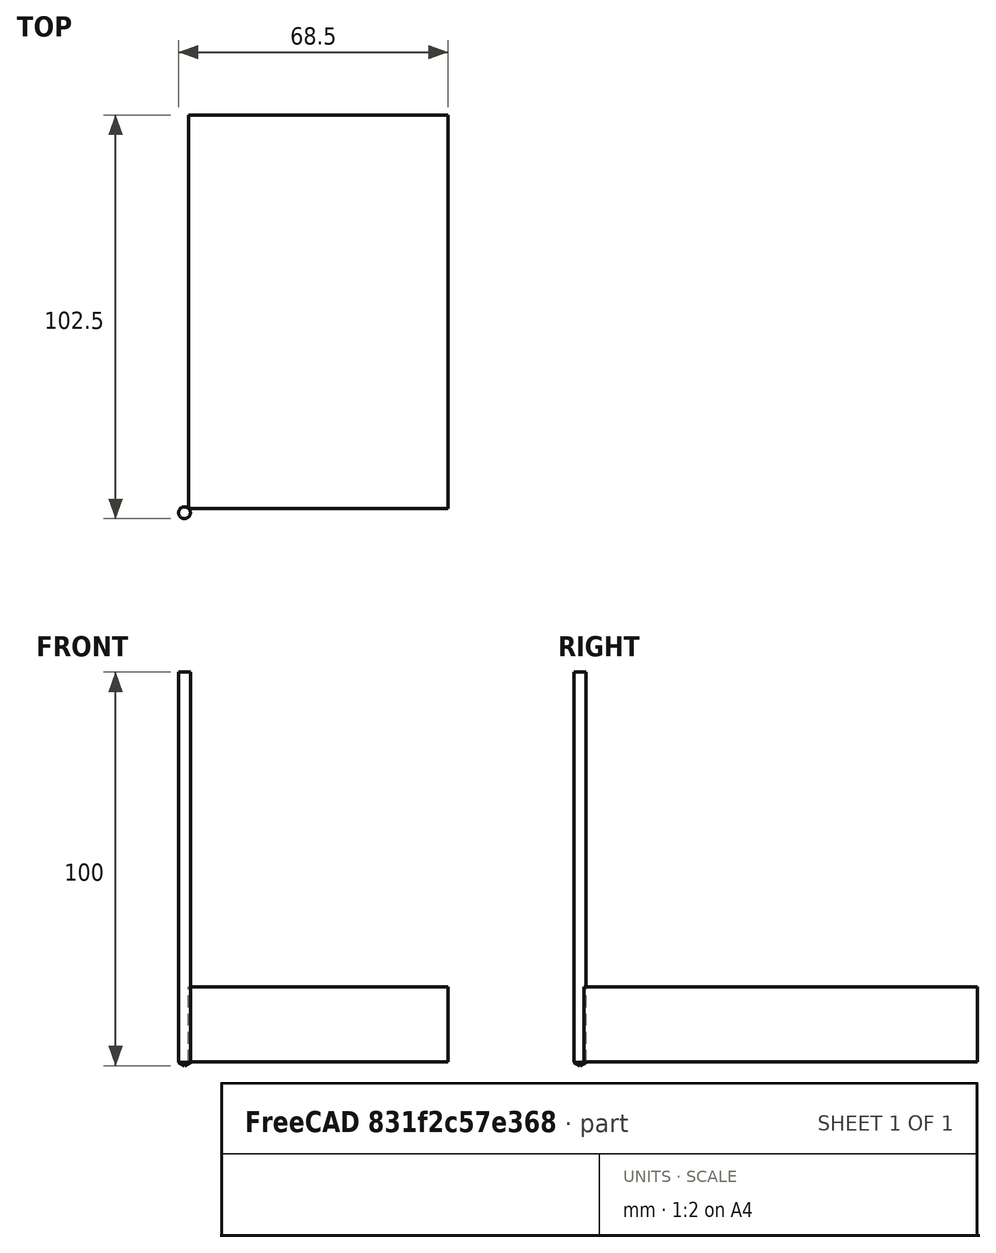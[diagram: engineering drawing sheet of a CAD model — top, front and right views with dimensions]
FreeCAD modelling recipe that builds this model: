
FCSTD DOCUMENT  (FreeCAD 1.0R39319 (Git))
Label: CNC test2
License: All rights reserved
LicenseURL: https://en.wikipedia.org/wiki/All_rights_reserved
objects: Path::FeaturePython×6, Sketcher::SketchObject×5, PartDesign::Pocket×4, Part::FeaturePython×3, App::DocumentObjectGroup×3, PartDesign::Pad×2, PartDesign::Body×1, App::FeaturePython×1, Mesh::Feature×1, Part::Feature×1, Part::Refine×1
note: 38 computed .brp shape members not serialized (recipe doc carries the construction recipe); baked Part::Feature solids carry a one-line shape summary decoded from their .brp

FEATURE [Sketcher::SketchObject] Sketch247
  ArcFitTolerance = 1e-06
  AttachmentSupport = -> [XY_Plane1079]
  FullyConstrained = true
  MakeInternals = false
  MapMode = 5
  sketch-geometry (14):
    g0: Circle [constr] CenterX=0 CenterY=0 CenterZ=0 NormalX=0 NormalY=0 NormalZ=1 AngleXU=0 Radius=12
    g1: LineSegment StartX=-3.45 StartY=2 StartZ=0 EndX=-3.45 EndY=18.25 EndZ=0
    g2: LineSegment StartX=-3.45 StartY=18.25 StartZ=0 EndX=3.45 EndY=18.25 EndZ=0
    g3: LineSegment StartX=3.45 StartY=18.25 StartZ=0 EndX=3.45 EndY=2 EndZ=0
    g4: LineSegment StartX=3.45 StartY=2 StartZ=0 EndX=9.95 EndY=2 EndZ=0
    g5: LineSegment StartX=9.95 StartY=2 StartZ=0 EndX=9.95 EndY=-2 EndZ=0
    g6: LineSegment StartX=9.95 StartY=-2 StartZ=0 EndX=3.45 EndY=-2 EndZ=0
    g7: LineSegment StartX=3.45 StartY=-2 StartZ=0 EndX=3.45 EndY=-18.25 EndZ=0
    g8: LineSegment StartX=3.45 StartY=-18.25 StartZ=0 EndX=-3.45 EndY=-18.25 EndZ=0
    g9: LineSegment StartX=-3.45 StartY=-18.25 StartZ=0 EndX=-3.45 EndY=-2 EndZ=0
    g10: LineSegment StartX=-3.45 StartY=-2 StartZ=0 EndX=-9.95 EndY=-2 EndZ=0
    g11: LineSegment StartX=-9.95 StartY=-2 StartZ=0 EndX=-9.95 EndY=2 EndZ=0
    g12: LineSegment StartX=-9.95 StartY=2 StartZ=0 EndX=-3.45 EndY=2 EndZ=0
    g13: Circle [constr] CenterX=0 CenterY=0 CenterZ=0 NormalX=0 NormalY=0 NormalZ=1 AngleXU=0 Radius=12
  constraints (39):
    c: Diameter(g0) = 24
    c: Coincident(g0,g-1)
    c: Vertical(g1)
    c: Coincident(g1,g2)
    c: Coincident(g2,g3)
    c: Vertical(g3)
    c: Coincident(g3,g4)
    c: Horizontal(g4)
    c: Coincident(g4,g5)
    c: Vertical(g5)
    c: Coincident(g5,g6)
    c: Horizontal(g6)
    c: Coincident(g6,g7)
    c: Vertical(g7)
    c: Coincident(g7,g8)
    c: Coincident(g8,g9)
    c: Vertical(g9)
    c: Coincident(g9,g10)
    c: Horizontal(g10)
    c: Coincident(g10,g11)
    c: Vertical(g11)
    c: Coincident(g11,g12)
    c: Coincident(g12,g1)
    c: Horizontal(g12)
    c: Horizontal(g8)
    c: Horizontal(g2)
    c: Equal(g3,g1)
    c: Equal(g1,g9)
    c: Equal(g9,g7)
    c: Equal(g6,g4)
    c: Equal(g4,g12)
    c: Equal(g12,g10)
    c: Distance(g2,g2) = 6.9
    c: DistanceY(g5,g5) = 4
    c: DistanceY(g3,g3) = 16.25
    c: DistanceX(g4,g4) = 6.5
    c: Symmetric(g1,g6,g0)
    c: Coincident(g13,g0)
    c: Equal(g13,g0)
FEATURE [PartDesign::Pad] Pad125
  Direction = (0,0,1)
  Length = 4
  Length2 = 10
  Profile = -> Sketch247
  ReferenceAxis = -> Sketch247 [N_Axis]
  Refine = true
  Suppressed = false
  Type = 0
FEATURE [Sketcher::SketchObject] Sketch248
  ArcFitTolerance = 1e-06
  AttachmentSupport = -> [Pad125]
  FullyConstrained = true
  MakeInternals = false
  MapMode = 5
  Placement = pos=(0,0,4) rot=(0,0,1;0rad)
  sketch-geometry (1):
    g0: Circle CenterX=0 CenterY=0 CenterZ=0 NormalX=0 NormalY=0 NormalZ=1 AngleXU=0 Radius=12
  constraints (2):
    c: Diameter(g0) = 24
    c: Coincident(g0,g-1)
FEATURE [PartDesign::Pad] Pad126
  BaseFeature = -> Pad125
  Direction = (0,0,1)
  Length = 12
  Length2 = 10
  Profile = -> Sketch248
  ReferenceAxis = -> Sketch248 [N_Axis]
  Refine = true
  Suppressed = false
  Type = 0
FEATURE [PartDesign::Pocket] Pocket089
  BaseFeature = -> Pad126
  Direction = (0,0,1)
  Length = 8
  Length2 = 5
  Profile = -> Pad126 [Face4]
  Refine = true
  Suppressed = false
  Type = 0
FEATURE [Sketcher::SketchObject] Sketch249
  ArcFitTolerance = 1e-06
  AttachmentSupport = -> [Pocket089]
  FullyConstrained = true
  MakeInternals = false
  MapMode = 5
  Placement = pos=(0,0,16) rot=(0,0,1;0rad)
  sketch-geometry (1):
    g0: Circle CenterX=0 CenterY=0 CenterZ=0 NormalX=0 NormalY=0 NormalZ=1 AngleXU=0 Radius=3.1
  constraints (2):
    c: Diameter(g0) = 6.2
    c: Coincident(g0,g-1)
FEATURE [PartDesign::Pocket] Pocket090
  BaseFeature = -> Pocket089
  Direction = (0,0,-1)
  Length = 5
  Length2 = 5
  Profile = -> Sketch249
  ReferenceAxis = -> Sketch249 [N_Axis]
  Refine = true
  Suppressed = false
  Type = 1
FEATURE [Sketcher::SketchObject] Sketch250
  ArcFitTolerance = 1e-06
  AttachmentSupport = -> [XZ_Plane1079]
  ExternalGeometry = -> [Pocket090]
  FullyConstrained = true
  MakeInternals = false
  MapMode = 5
  Placement = pos=(0,0,0) rot=(1,0,0;1.5708rad)
  sketch-geometry (1):
    g0: Circle CenterX=1e-16 CenterY=12 CenterZ=0 NormalX=0 NormalY=0 NormalZ=1 AngleXU=0 Radius=2.35
  constraints (2):
    c: Diameter(g0) = 4.7
    c: Symmetric(g-4,g-3,g0)
FEATURE [PartDesign::Pocket] Pocket091
  BaseFeature = -> Pocket090
  Direction = (0,1,-2e-16)
  Length = 5
  Length2 = 5
  Profile = -> Sketch250
  ReferenceAxis = -> Sketch250 [N_Axis]
  Refine = true
  Suppressed = false
  Type = 1
FEATURE [Sketcher::SketchObject] Sketch251
  ArcFitTolerance = 1e-06
  AttachmentSupport = -> [Pocket091]
  ExternalGeometry = -> [Pocket091]
  FullyConstrained = false
  MakeInternals = false
  MapMode = 5
  Placement = pos=(0,0,16) rot=(0,0,1;0rad)
  sketch-geometry (4):
    g0: LineSegment StartX=-5 StartY=10.9087 StartZ=0 EndX=5 EndY=10.9087 EndZ=0
    g1: LineSegment StartX=5 StartY=10.9087 StartZ=0 EndX=5 EndY=16.9794 EndZ=0
    g2: LineSegment StartX=5 StartY=16.9794 StartZ=0 EndX=-5 EndY=16.9794 EndZ=0
    g3: LineSegment StartX=-5 StartY=16.9794 StartZ=0 EndX=-5 EndY=10.9087 EndZ=0
  constraints (11):
    c: Coincident(g0,g1)
    c: Coincident(g1,g2)
    c: Coincident(g2,g3)
    c: Coincident(g3,g0)
    c: Horizontal(g0)
    c: Horizontal(g2)
    c: Vertical(g1)
    c: Vertical(g3)
    c: PointOnObject(g0,g-3)
    c: PointOnObject(g0,g-3)
    c: Distance(g0,g0) = 10
FEATURE [PartDesign::Pocket] Pocket092
  BaseFeature = -> Pocket091
  Direction = (0,0,-1)
  Length = 5
  Length2 = 5
  Profile = -> Sketch251
  ReferenceAxis = -> Sketch251 [N_Axis]
  Refine = true
  Suppressed = false
  Type = 1
FEATURE [PartDesign::Body] Body142  label="Servo to pot"
  AllowCompound = false
  Group = -> [Sketch247,Pad125,Sketch248,Pad126,Pocket089,Sketch249,Pocket090,Sketch250,Pocket091,Sketch251,Pocket092]
  Origin = -> Origin1488
  Placement = pos=(0,-90,0) rot=(-1,0,0;3.14159rad)
  Tip = -> Pocket092
FEATURE [App::FeaturePython] SetupSheet  # Path/CAM operation (typed FeaturePython)
  ClearanceHeightExpression = OpStockZMax+SetupSheet.ClearanceHeightOffset
  ClearanceHeightOffset = 5
  CoolantMode = 0
  CoolantModes = None | Flood | Mist
  FinalDepthExpression = OpFinalDepth
  HorizRapid = 700
  SafeHeightExpression = OpStockZMax+SetupSheet.SafeHeightOffset
  SafeHeightOffset = 3
  StartDepthExpression = OpStartDepth
  StepDownExpression = .5mm
  VertRapid = 700
FEATURE [Part::FeaturePython] Clone  label="Model-Servo to pot"  # Draft clone (typed FeaturePython)
  AttacherType = Attacher::AttachEngine3D
  Fuse = false
  Objects = -> [Body142]
  PathResource = Model
  Placement = pos=(12.9714,11.9087,17) rot=(-1,0,0;3.14159rad)
  Scale = (1,1,1)
FEATURE [App::DocumentObjectGroup] Model
  Group = -> [Clone]
FEATURE [Part::FeaturePython] ToolBit  label="3mm_Drill"  # Path/CAM toolbit (typed FeaturePython)
  BitPropertyNames = Chipload | Diameter | Flutes | Length | Material | TipAngle
  BitShape = <path>
  Chipload = 0
  Diameter = 3
  File = <userpath>/.local/share/FreeCAD/Tools/Bit/3mm_Drill.fctb
  Flutes = 0
  Length = 100
  Material = 0
  ShapeName = drill
  TipAngle = 119
FEATURE [Path::FeaturePython] TC__3mm_Drill  label="TC: 3mm_Drill"  # Path/CAM operation (typed FeaturePython)
  HorizFeed = 500
  HorizRapid = 700
  SpindleDir = 0
  SpindleSpeed = 4000
  Tool = -> ToolBit
  ToolNumber = 1
  VertFeed = 400
  VertRapid = 700
  expr: HorizRapid = SetupSheet.HorizRapid
  expr: VertRapid = SetupSheet.VertRapid
FEATURE [App::DocumentObjectGroup] Tools
  Group = -> [TC__3mm_Drill]
FEATURE [Path::FeaturePython] Pocket_Shape  # Path/CAM operation (typed FeaturePython)
  Active = true
  AreaParams:
    Tolerance = 1e-07
    FitArcs = True
    Simplify = False
    CleanDistance = 0.0
    Accuracy = 0.01
    Unit = 1.0
    MinArcPoints = 4
    MaxArcPoints = 100
    ClipperScale = 10000000.0
    Fill = 0
    Coplanar = 0
    Reorient = True
    Outline = False
    Explode = False
    OpenMode = 0
    Deflection = 0.01
    SubjectFill = 0
    ClipFill = 0
    Offset = 0.0
    ExtraPass = 0
    Stepover = 0.0
    LastStepover = 0.0
    JoinType = 0
    EndType = 0
    MiterLimit = 2.0
    RoundPrecision = 0.0
    PocketMode = 2
    ToolRadius = 1.5
    PocketExtraOffset = 0.0
    PocketStepover = 3.0
    PocketLastStepover = 0.0
    FromCenter = True
    Angle = 45.0
    AngleShift = 0.0
    Shift = 0.0
    Thicken = False
    SectionCount = -1
    Stepdown = 1.0
    SectionOffset = 0.0
    SectionTolerance = 1e-06
    SectionMode = 2
    Project = False
  Base = -> [Clone]
  ClearanceHeight = 25
  CoolantMode = 0
  CutMode = 0
  CycleTime = 00:00:03
  ExtensionCorners = true
  ExtensionLengthDefault = 1.5
  ExtraOffset = 0
  FinalDepth = 9
  FinishDepth = 0
  KeepToolDown = false
  MinTravel = true
  OffsetPattern = 1
  OpFinalDepth = 9
  OpStartDepth = 20
  OpStockZMax = 20
  OpStockZMin = 1
  OpToolDiameter = 3
  PathParams = {'orientation': 1, 'sort_mode': 3, 'threshold': 3.0, 'feedrate': 500.0, 'feedrate_v': 400.0, 'verbose': True, 'resume_height': 23.0, 'retraction': 25.0, 'return_end': True, 'preamble': False, 'start': Vector (0.0, 0.0, 0.0)}
  PocketLastStepOver = 0
  SafeHeight = 23
  SplitArcs = false
  StartAt = 0
  StartDepth = 20
  StartPoint = (0,0,0)
  StepDown = 0.5
  StepOver = 100
  ToolController = -> TC__3mm_Drill
  UseOutline = true
  UseRestMachining = true
  UseStartPoint = true
  ZigZagAngle = 45
  expr: ClearanceHeight = OpStockZMax + SetupSheet.ClearanceHeightOffset
  expr: ExtensionLengthDefault = OpToolDiameter / 2
  expr: FinalDepth = OpFinalDepth
  expr: SafeHeight = OpStockZMax + SetupSheet.SafeHeightOffset
  expr: StartDepth = OpStartDepth
  expr: StepDown = 0.5 mm
FEATURE [Path::FeaturePython] Pocket_Shape001  # Path/CAM operation (typed FeaturePython)
  Active = true
  AreaParams:
    Tolerance = 1e-07
    FitArcs = True
    Simplify = False
    CleanDistance = 0.0
    Accuracy = 0.01
    Unit = 1.0
    MinArcPoints = 4
    MaxArcPoints = 100
    ClipperScale = 10000000.0
    Fill = 0
    Coplanar = 0
    Reorient = True
    Outline = False
    Explode = False
    OpenMode = 0
    Deflection = 0.01
    SubjectFill = 0
    ClipFill = 0
    Offset = 0.0
    ExtraPass = 0
    Stepover = 0.0
    LastStepover = 0.0
    JoinType = 0
    EndType = 0
    MiterLimit = 2.0
    RoundPrecision = 0.0
    PocketMode = 2
    ToolRadius = 1.5
    PocketExtraOffset = 0.0
    PocketStepover = 3.0
    PocketLastStepover = 0.0
    FromCenter = True
    Angle = 45.0
    AngleShift = 0.0
    Shift = 0.0
    Thicken = False
    SectionCount = -1
    Stepdown = 1.0
    SectionOffset = 0.0
    SectionTolerance = 1e-06
    SectionMode = 2
    Project = False
  Base = -> [Clone]
  ClearanceHeight = 25
  CoolantMode = 0
  CutMode = 0
  CycleTime = 00:00:00
  ExtensionCorners = true
  ExtensionLengthDefault = 1.5
  ExtraOffset = 0
  FinalDepth = 1
  FinishDepth = 0
  KeepToolDown = false
  MinTravel = true
  OffsetPattern = 1
  OpFinalDepth = 1
  OpStartDepth = 20
  OpStockZMax = 20
  OpStockZMin = 1
  OpToolDiameter = 3
  PathParams = {'orientation': 1, 'feedrate': 500.0, 'feedrate_v': 400.0, 'verbose': True, 'resume_height': 23.0, 'retraction': 25.0, 'return_end': True, 'preamble': False}
  PocketLastStepOver = 0
  SafeHeight = 23
  SplitArcs = false
  StartAt = 0
  StartDepth = 20
  StartPoint = (0,0,0)
  StepDown = 0.5
  StepOver = 100
  ToolController = -> TC__3mm_Drill
  UseOutline = false
  UseRestMachining = true
  UseStartPoint = false
  ZigZagAngle = 45
  expr: ClearanceHeight = OpStockZMax + SetupSheet.ClearanceHeightOffset
  expr: ExtensionLengthDefault = OpToolDiameter / 2
  expr: FinalDepth = OpFinalDepth
  expr: SafeHeight = OpStockZMax + SetupSheet.SafeHeightOffset
  expr: StartDepth = OpStartDepth
  expr: StepDown = 0.5 mm
FEATURE [Path::FeaturePython] Profile  # Path/CAM operation (typed FeaturePython)
  Active = true
  AreaParams:
    Tolerance = 1e-07
    FitArcs = True
    Simplify = False
    CleanDistance = 0.0
    Accuracy = 0.01
    Unit = 1.0
    MinArcPoints = 4
    MaxArcPoints = 100
    ClipperScale = 10000000.0
    Fill = 0
    Coplanar = 0
    Reorient = True
    Outline = False
    Explode = False
    OpenMode = 0
    Deflection = 0.01
    SubjectFill = 0
    ClipFill = 0
    Offset = 1.5
    ExtraPass = 0
    Stepover = 0.0
    LastStepover = 0.0
    JoinType = 0
    EndType = 0
    MiterLimit = 2.0
    RoundPrecision = 0.0
    PocketMode = 0
    ToolRadius = 1.0
    PocketExtraOffset = 0.0
    PocketStepover = 0.0
    PocketLastStepover = 0.0
    FromCenter = False
    Angle = 45.0
    AngleShift = 0.0
    Shift = 0.0
    Thicken = False
    SectionCount = -1
    Stepdown = 1.0
    SectionOffset = 0.0
    SectionTolerance = 1e-06
    SectionMode = 2
    Project = False
  Base = -> [Clone]
  ClearanceHeight = 25
  CoolantMode = 0
  CycleTime = 00:00:05
  Direction = 0
  FinalDepth = 1
  HandleMultipleFeatures = 0
  JoinType = 0
  MiterLimit = 0.1
  OffsetExtra = 0
  OpFinalDepth = 1
  OpStartDepth = 20
  OpStockZMax = 20
  OpStockZMin = 1
  OpToolDiameter = 3
  PathParams = {'orientation': 1, 'feedrate': 500.0, 'feedrate_v': 400.0, 'verbose': True, 'resume_height': 23.0, 'retraction': 25.0, 'return_end': True, 'preamble': False}
  SafeHeight = 23
  Side = 0
  SplitArcs = false
  StartDepth = 20
  StartPoint = (0,0,0)
  StepDown = 0.5
  ToolController = -> TC__3mm_Drill
  UseComp = true
  UseStartPoint = false
  processCircles = false
  processHoles = false
  processPerimeter = true
  expr: ClearanceHeight = OpStockZMax + SetupSheet.ClearanceHeightOffset
  expr: FinalDepth = OpFinalDepth
  expr: SafeHeight = OpStockZMax + SetupSheet.SafeHeightOffset
  expr: StartDepth = OpStartDepth
  expr: StepDown = 0.5 mm
FEATURE [Part::FeaturePython] Stock001  # WARN: FeaturePython — macro-defined, semantics opaque (R4)
  Height = 19
  Length = 66
  Placement = pos=(1,1,1) rot=(0,0,1;0rad)
  StockType = CreateBox
  Width = 100
FEATURE [Path::FeaturePython] MillFace  # Path/CAM operation (typed FeaturePython)
  Active = true
  AreaParams:
    Tolerance = 1e-07
    FitArcs = True
    Simplify = False
    CleanDistance = 0.0
    Accuracy = 0.01
    Unit = 1.0
    MinArcPoints = 4
    MaxArcPoints = 100
    ClipperScale = 10000000.0
    Fill = 0
    Coplanar = 0
    Reorient = True
    Outline = False
    Explode = False
    OpenMode = 0
    Deflection = 0.01
    SubjectFill = 0
    ClipFill = 0
    Offset = 0.0
    ExtraPass = 0
    Stepover = 0.0
    LastStepover = 0.0
    JoinType = 0
    EndType = 0
    MiterLimit = 2.0
    RoundPrecision = 0.0
    PocketMode = 2
    ToolRadius = 1.5
    PocketExtraOffset = 0.0
    PocketStepover = 1.2000000000000002
    PocketLastStepover = 0.0
    FromCenter = True
    Angle = 45.0
    AngleShift = 0.0
    Shift = 0.0
    Thicken = False
    SectionCount = -1
    Stepdown = 1.0
    SectionOffset = 0.0
    SectionTolerance = 1e-06
    SectionMode = 2
    Project = False
  Base = -> [Clone]
  BoundaryShape = 0
  ClearEdges = false
  ClearanceHeight = 25
  CoolantMode = 0
  CutMode = 0
  CycleTime = 00:00:15
  ExcludeRaisedAreas = false
  ExtraOffset = 0
  FinalDepth = 13
  FinishDepth = 0
  KeepToolDown = false
  MinTravel = false
  OffsetPattern = 1
  OpFinalDepth = 13
  OpStartDepth = 20
  OpStockZMax = 20
  OpStockZMin = 1
  OpToolDiameter = 3
  PathParams = {'orientation': 1, 'feedrate': 500.0, 'feedrate_v': 400.0, 'verbose': True, 'resume_height': 23.0, 'retraction': 25.0, 'return_end': True, 'preamble': False, 'sort_mode': 0}
  PocketLastStepOver = 0
  SafeHeight = 23
  SplitArcs = false
  StartAt = 0
  StartDepth = 20
  StartPoint = (0,0,0)
  StepDown = 0.5
  StepOver = 40
  ToolController = -> TC__3mm_Drill
  UseRestMachining = false
  UseStartPoint = false
  ZigZagAngle = 45
  expr: ClearanceHeight = OpStockZMax + SetupSheet.ClearanceHeightOffset
  expr: FinalDepth = OpFinalDepth
  expr: SafeHeight = OpStockZMax + SetupSheet.SafeHeightOffset
  expr: StartDepth = OpStartDepth
  expr: StepDown = 0.5 mm
FEATURE [App::DocumentObjectGroup] Operations
  Group = -> [MillFace,Pocket_Shape,Pocket_Shape001,Profile]
FEATURE [Path::FeaturePython] Job  # Path/CAM operation (typed FeaturePython)
  CycleTime = 00:00:23
  Fixtures = G54
  GeometryTolerance = 0.01
  JobType = 0
  Model = -> Model
  Operations = -> Operations
  OrderOutputBy = 2
  PostProcessor = 16
  SetupSheet = -> SetupSheet
  SplitOutput = true
  Stock = -> Stock001
  Tools = -> Tools
FEATURE [Mesh::Feature] sponge_holder_v2  label="sponge-holder-v2"
FEATURE [Part::Feature] sponge_holder_v003
  shape: bbox 110 x 90 x 22 mm, 21932 faces, 0 solids (baked)
FEATURE [Part::Refine] sponge_holder_v004
  Source = -> sponge_holder_v003
note: 1 file-system path scrubbed to <path> (originals preserved in the JSON sidecar)
